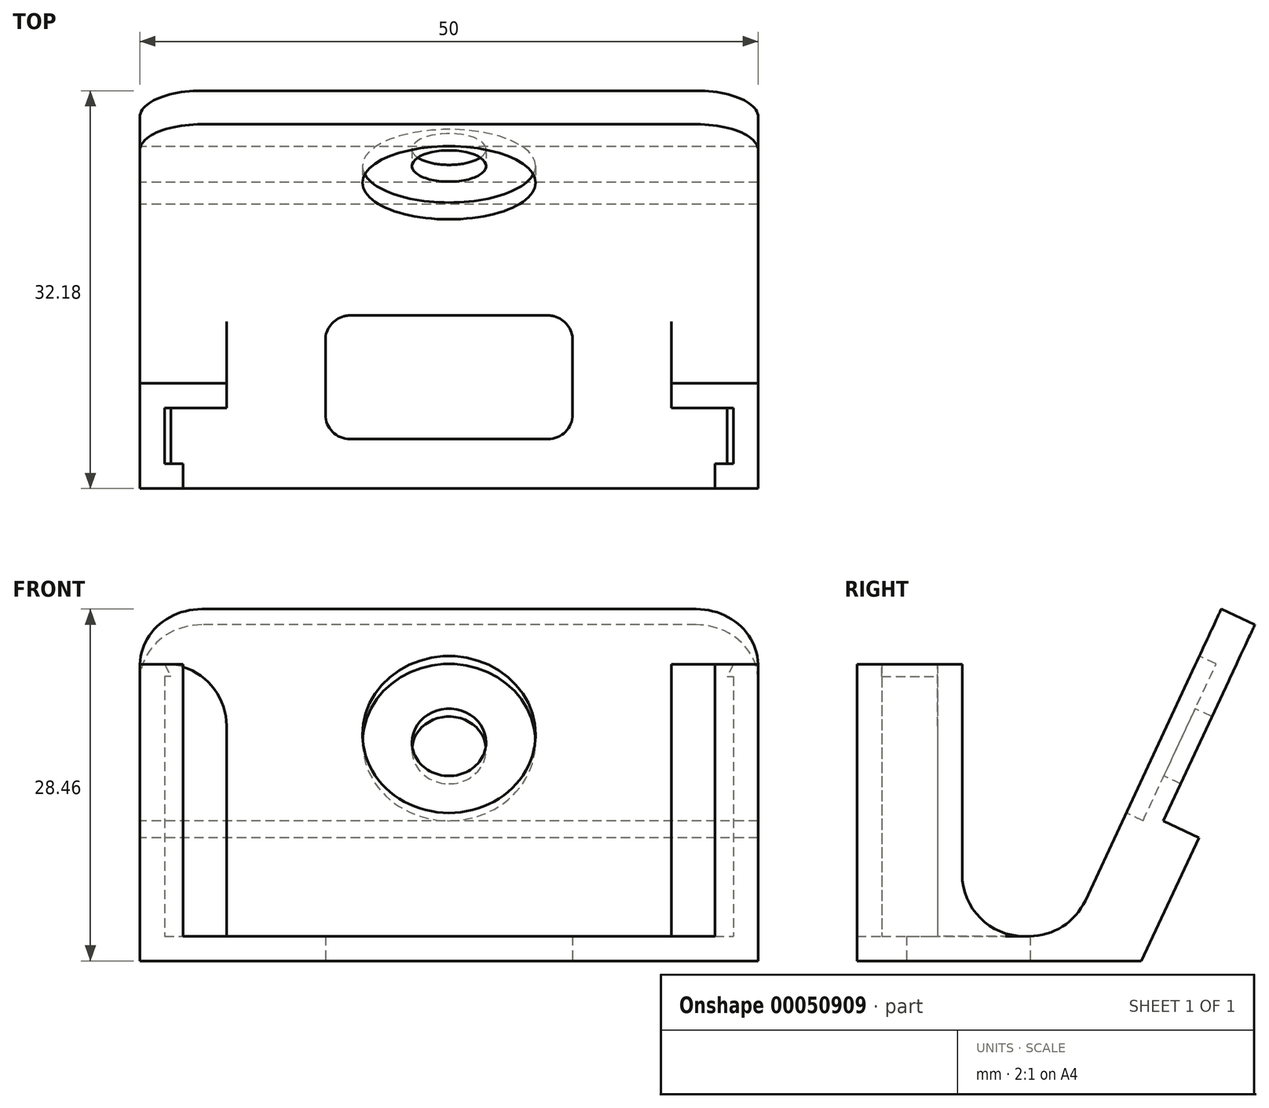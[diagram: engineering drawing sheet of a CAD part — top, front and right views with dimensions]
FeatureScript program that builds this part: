
annotation { "Feature Type Name" : "Feature", "Feature Type Description" : "" }
export const myFeature = defineFeature(function(context is Context, id is Id, definition is map)
    precondition{}
    {
        {
            var Q0;
            Q0=qCreatedBy(makeId("Right.planeOp"),FACE);
            var sketch = newSketch(context, id + "F0", { "sketchPlane" : qUnion([Q0])});
            skLineSegment(sketch, "E0.bottom", {"start": v(0, 0) * mm, "end": v(-2, 0) * mm});
            skLineSegment(sketch, "E0.top", {"start": v(0, 24) * mm, "end": v(-2, 24) * mm});
            skLineSegment(sketch, "E0.left", {"start": v(0, 0) * mm, "end": v(0, 24) * mm});
            skLineSegment(sketch, "E0.right", {"start": v(-2, 0) * mm, "end": v(-2, 24) * mm});
            skLineSegment(sketch, "E1.bottom", {"start": v(0, 0) * mm, "end": v(11, 0) * mm});
            skLineSegment(sketch, "E1.top", {"start": v(0, 2) * mm, "end": v(8.62, 2) * mm});
            skLineSegment(sketch, "E1.left", {"start": v(0, 0) * mm, "end": v(0, 2) * mm});
            skLineSegment(sketch, "E2.top", {"start": v(20.96, 28.46) * mm, "end": v(23.68, 27.19) * mm});
            skLineSegment(sketch, "E2.left", {"start": v(8.62, 2) * mm, "end": v(20.96, 28.46) * mm});
            skLineSegment(sketch, "E2.right", {"start": v(11, 0) * mm, "end": v(23.68, 27.19) * mm});
            skLineSegment(sketch, "E3", {"start": v(11, 0) * mm, "end": v(14.5, 0) * mm});
            skLineSegment(sketch, "E4", {"start": v(14.5, 0) * mm, "end": v(19.15, 9.97) * mm});
            skLineSegment(sketch, "E5", {"start": v(19.15, 9.97) * mm, "end": v(16.27, 11.31) * mm});
            skSolve(sketch);
        }
        {
            var Q0;
            Q0=makeQuery(id+"F0.imprint","IMPRINT",FACE,{"disambiguationData":[TD([[makeQuery(id+"F0.imprint","IMPRINT",EDGE,{"derivedFrom":sQuery(id+"F0.wireOp",EDGE,"E0.bottom")}),-1.0]])]});
            var Q1;
            Q1=makeQuery(id+"F0.imprint","IMPRINT",FACE,{"disambiguationData":[TD([[makeQuery(id+"F0.imprint","IMPRINT",EDGE,{"derivedFrom":sQuery(id+"F0.wireOp",EDGE,"E1.bottom")}),1.0]])]});
            var Q2;
            {var subQ0=sQuery(id+"F0.wireOp",EDGE,"E3");Q2=makeQuery(id+"F0.imprint","IMPRINT",FACE,{"disambiguationData":[TD([[makeQuery(id+"F0.imprint","IMPRINT",EDGE,{"derivedFrom":subQ0}),1.0]])]});}
            extrude(context, id + "F1", {"entities" : qUnion([Q0, Q1, Q2]), "depth" : 50 * mm});
        }
        {
            var Q0;
            Q0=makeQuery(id+"F1.opExtrude","SWEPT_FACE",FACE,{"disambiguationData":[OSD([sQuery(id+"F0.wireOp",EDGE,"E2.left")])]});
            var sketch = newSketch(context, id + "F2", { "sketchPlane" : qUnion([Q0])});
            skCircle(sketch, "E6", {"center": v(25, 23.46) * mm, "radius": 3 * mm});
            skLineSegment(sketch, "E7", {"start": v(0, 23.46) * mm, "end": v(50, 23.46) * mm});
            skSolve(sketch);
        }
        {
            var Q0;
            {var subQ0=sQuery(id+"F2.wireOp",EDGE,"E7");var subQ1=sQuery(id+"F2.wireOp",EDGE,"E6");var subQ2=makeQuery(id+"F2.imprint","INTERSECT",VERTEX,{"disambiguationData":[OD(0.0)],"derivedFrom":[subQ1,subQ0]});Q0=makeQuery(id+"F2.imprint","IMPRINT",FACE,{"disambiguationData":[TD([[makeQuery(id+"F2.imprint","IMPRINT",EDGE,{"disambiguationData":[TD([[subQ2,1.0]])],"derivedFrom":subQ1}),1.0]])]});}
            var Q1;
            {var subQ0=sQuery(id+"F2.wireOp",EDGE,"E7");var subQ1=sQuery(id+"F2.wireOp",EDGE,"E6");var subQ2=makeQuery(id+"F2.imprint","INTERSECT",VERTEX,{"disambiguationData":[OD(0.0)],"derivedFrom":[subQ1,subQ0]});Q1=makeQuery(id+"F2.imprint","IMPRINT",FACE,{"disambiguationData":[TD([[makeQuery(id+"F2.imprint","IMPRINT",EDGE,{"disambiguationData":[TD([[subQ2,-1.0]])],"derivedFrom":subQ1}),1.0]])]});}
            extrude(context, id + "F3", {"entities" : qUnion([Q0, Q1]), "operationType" : NewBodyOperationType.REMOVE, "endBound" : BoundingType.UP_TO_NEXT, "oppositeDirection" : true, "depth" : 25.4 * mm});
        }
        {
            var Q0;
            Q0=makeQuery(id+"F1.opExtrude","SWEPT_FACE",FACE,{"disambiguationData":[OSD([sQuery(id+"F0.wireOp",EDGE,"E0.right")])]});
            var sketch = newSketch(context, id + "F4", { "sketchPlane" : qUnion([Q0])});
            skLineSegment(sketch, "E8", {"start": v(2, 24) * mm, "end": v(2, 2) * mm});
            skLineSegment(sketch, "E9", {"start": v(2, 2) * mm, "end": v(48, 2) * mm});
            skLineSegment(sketch, "E10", {"start": v(48, 2) * mm, "end": v(48, 24) * mm});
            skSolve(sketch);
        }
        {
            var Q0;
            {var subQ3=sQuery(id+"F4.wireOp",EDGE,"E8");Q0=makeQuery(id+"F4.imprint","IMPRINT",FACE,{"disambiguationData":[TD([[makeQuery(id+"F4.imprint","IMPRINT",EDGE,{"derivedFrom":subQ3}),-1.0]])]});}
            extrude(context, id + "F5", {"entities" : qUnion([Q0]), "operationType" : NewBodyOperationType.ADD, "depth" : 6.5 * mm});
        }
        {
            var Q0;
            Q0=makeQuery(id+"F5.opExtrude","SWEPT_FACE",FACE,{"disambiguationData":[OSD([sQuery(id+"F4.wireOp",EDGE,"E8")])]});
            var sketch = newSketch(context, id + "F6", { "sketchPlane" : qUnion([Q0])});
            skLineSegment(sketch, "E11", {"start": v(-6.5, 24) * mm, "end": v(-6.5, 2) * mm});
            skSolve(sketch);
        }
        {
            var Q0;
            {var subQ0=sQuery(id+"F6.wireOp",EDGE,"E11");Q0=makeQuery(id+"F6.imprint","IMPRINT",FACE,{"disambiguationData":[TD([[makeQuery(id+"F6.imprint","IMPRINT",EDGE,{"derivedFrom":subQ0}),-1.0]])]});}
            var Q1;
            Q1=makeQuery(id+"F5.opExtrude","SWEPT_FACE",FACE,{"disambiguationData":[OSD([sQuery(id+"F4.wireOp",EDGE,"E10")])]});
            extrude(context, id + "F7", {"entities" : qUnion([Q0, Q1]), "operationType" : NewBodyOperationType.ADD, "depth" : 1.5 * mm});
        }
        {
            var Q0;
            Q0=makeQuery(id+"F5.opExtrude","SWEPT_FACE",FACE,{"disambiguationData":[OSD([sQuery(id+"F4.wireOp",EDGE,"E10")])]});
            var sketch = newSketch(context, id + "F8", { "sketchPlane" : qUnion([Q0])});
            skLineSegment(sketch, "E12", {"start": v(6.5, 24) * mm, "end": v(6.5, 2) * mm});
            skSolve(sketch);
        }
        {
            var Q0;
            {var subQ0=sQuery(id+"F8.wireOp",EDGE,"E12");Q0=makeQuery(id+"F8.imprint","IMPRINT",FACE,{"disambiguationData":[TD([[makeQuery(id+"F8.imprint","IMPRINT",EDGE,{"derivedFrom":subQ0}),1.0]])]});}
            extrude(context, id + "F9", {"entities" : qUnion([Q0]), "operationType" : NewBodyOperationType.ADD, "depth" : 1.5 * mm});
        }
        {
            var Q0;
            Q0=makeQuery(id+"F1.opExtrude","SWEPT_FACE",FACE,{"disambiguationData":[OSD([sQuery(id+"F0.wireOp",EDGE,"E0.right")])]});
            var sketch = newSketch(context, id + "F10", { "sketchPlane" : qUnion([Q0])});
            skLineSegment(sketch, "E13", {"start": v(7, 24) * mm, "end": v(7, 2) * mm});
            skLineSegment(sketch, "E14", {"start": v(43, 24) * mm, "end": v(43, 2) * mm});
            skSolve(sketch);
        }
        {
            var Q0;
            {var subQ0=sQuery(id+"F10.wireOp",EDGE,"E13");Q0=makeQuery(id+"F10.imprint","IMPRINT",FACE,{"disambiguationData":[TD([[makeQuery(id+"F10.imprint","IMPRINT",EDGE,{"derivedFrom":subQ0}),1.0]])]});}
            extrude(context, id + "F11", {"entities" : qUnion([Q0]), "operationType" : NewBodyOperationType.REMOVE, "oppositeDirection" : true, "depth" : 2 * mm});
        }
        {
            var Q0;
            Q0=qCreatedBy(makeId("Top.planeOp"),FACE);
            var sketch = newSketch(context, id + "F12", { "sketchPlane" : qUnion([Q0])});
            skLineSegment(sketch, "E15.bottom", {"start": v(15, 5.5) * mm, "end": v(35, 5.5) * mm});
            skLineSegment(sketch, "E15.top", {"start": v(15, -4.5) * mm, "end": v(35, -4.5) * mm});
            skLineSegment(sketch, "E15.left", {"start": v(15, 5.5) * mm, "end": v(15, -4.5) * mm});
            skLineSegment(sketch, "E15.right", {"start": v(35, 5.5) * mm, "end": v(35, -4.5) * mm});
            skSolve(sketch);
        }
        {
            var Q0;
            Q0=makeQuery(id+"F12.imprint","IMPRINT",FACE,{"disambiguationData":[TD([[makeQuery(id+"F12.imprint","IMPRINT",EDGE,{"derivedFrom":sQuery(id+"F12.wireOp",EDGE,"E15.bottom")}),-1.0]])]});
            extrude(context, id + "F13", {"entities" : qUnion([Q0]), "operationType" : NewBodyOperationType.REMOVE, "endBound" : BoundingType.THROUGH_ALL, "depth" : 25.4 * mm});
        }
        {
            var Q0;
            Q0=makeQuery(id+"F1.opExtrude","SWEPT_EDGE",EDGE,{"disambiguationData":[OSD([sQuery(id+"F0.wireOp",EDGE,"E1.top"),sQuery(id+"F0.wireOp",EDGE,"E2.left")])]});
            fillet(context, id + "F14", {"entities" : qUnion([Q0]), "radius" : 5 * mm, "tangentPropagation" : true, "allowEdgeOverflow" : false});
        }
        {
            var Q0;
            {var subQ1=sQuery(id+"F0.wireOp",EDGE,"E1.top");var subQ2=sQuery(id+"F0.wireOp",EDGE,"E0.left");Q0=makeQuery(id+"F11.boolean.opBoolean","SPLIT",EDGE,{"disambiguationData":[TD([makeQuery(id+"F11.opExtrude","SWEPT_FACE",FACE,{"disambiguationData":[OSD([sQuery(id+"F10.wireOp",EDGE,"E13")])]})])],"derivedFrom":makeQuery(id+"F1.opExtrude","SWEPT_EDGE",EDGE,{"disambiguationData":[OSD([subQ2,subQ1,sQuery(id+"F0.wireOp",EDGE,"E1.left")])]})});}
            var Q1;
            {var subQ1=sQuery(id+"F0.wireOp",EDGE,"E1.top");var subQ2=sQuery(id+"F0.wireOp",EDGE,"E0.left");Q1=makeQuery(id+"F11.boolean.opBoolean","SPLIT",EDGE,{"disambiguationData":[TD([makeQuery(id+"F11.opExtrude","SWEPT_FACE",FACE,{"disambiguationData":[OSD([sQuery(id+"F10.wireOp",EDGE,"E14")])]})])],"derivedFrom":makeQuery(id+"F1.opExtrude","SWEPT_EDGE",EDGE,{"disambiguationData":[OSD([subQ2,subQ1,sQuery(id+"F0.wireOp",EDGE,"E1.left")])]})});}
            fillet(context, id + "F15", {"entities" : qUnion([Q0, Q1]), "radius" : 5 * mm, "tangentPropagation" : true, "allowEdgeOverflow" : false});
        }
        {
            var Q0;
            Q0=makeQuery(id+"F13.boolean.opBoolean","COPY",EDGE,{"derivedFrom":makeQuery(id+"F13.opExtrude","SWEPT_EDGE",EDGE,{"disambiguationData":[OSD([sQuery(id+"F12.wireOp",EDGE,"E15.bottom"),sQuery(id+"F12.wireOp",EDGE,"E15.right")])]})});
            fillet(context, id + "F16", {"entities" : qUnion([Q0]), "radius" : 2 * mm, "tangentPropagation" : true, "allowEdgeOverflow" : false});
        }
        {
            var Q0;
            Q0=makeQuery(id+"F13.boolean.opBoolean","COPY",EDGE,{"derivedFrom":makeQuery(id+"F13.opExtrude","SWEPT_EDGE",EDGE,{"disambiguationData":[OSD([sQuery(id+"F12.wireOp",EDGE,"E15.bottom"),sQuery(id+"F12.wireOp",EDGE,"E15.left")])]})});
            var Q1;
            Q1=makeQuery(id+"F13.boolean.opBoolean","COPY",EDGE,{"derivedFrom":makeQuery(id+"F13.opExtrude","SWEPT_EDGE",EDGE,{"disambiguationData":[OSD([sQuery(id+"F12.wireOp",EDGE,"E15.top"),sQuery(id+"F12.wireOp",EDGE,"E15.left")])]})});
            fillet(context, id + "F17", {"entities" : qUnion([Q0, Q1]), "radius" : 2 * mm, "tangentPropagation" : true, "allowEdgeOverflow" : false});
        }
        {
            var Q0;
            Q0=makeQuery(id+"F13.boolean.opBoolean","COPY",EDGE,{"derivedFrom":makeQuery(id+"F13.opExtrude","SWEPT_EDGE",EDGE,{"disambiguationData":[OSD([sQuery(id+"F12.wireOp",EDGE,"E15.top"),sQuery(id+"F12.wireOp",EDGE,"E15.right")])]})});
            fillet(context, id + "F18", {"entities" : qUnion([Q0]), "radius" : 2 * mm, "tangentPropagation" : true, "allowEdgeOverflow" : false});
        }
        {
            var Q0;
            Q0=makeQuery(id+"F1.opExtrude","SWEPT_FACE",FACE,{"disambiguationData":[OSD([sQuery(id+"F0.wireOp",EDGE,"E2.left")])]});
            var sketch = newSketch(context, id + "F19", { "sketchPlane" : qUnion([Q0])});
            skCircle(sketch, "E16", {"center": v(25, 23.46) * mm, "radius": 7 * mm});
            skSolve(sketch);
        }
        {
            var Q0;
            Q0=makeQuery(id+"F19.imprint","IMPRINT",FACE,{"disambiguationData":[TD([[makeQuery(id+"F19.imprint","IMPRINT",EDGE,{"derivedFrom":sQuery(id+"F19.wireOp",EDGE,"E16")}),1.0]])]});
            extrude(context, id + "F20", {"entities" : qUnion([Q0]), "operationType" : NewBodyOperationType.REMOVE, "oppositeDirection" : true, "depth" : 1.5 * mm});
        }
        {
            var Q0;
            {var subQ0=sQuery(id+"F4.wireOp",EDGE,"E10");var subQ3=sQuery(id+"F0.wireOp",EDGE,"E0.right");Q0=makeQuery(id+"F11.boolean.opBoolean","SPLIT",FACE,{"disambiguationData":[TD([makeQuery(id+"F5.opExtrude","SWEPT_FACE",FACE,{"disambiguationData":[OSD([subQ0])]})])],"derivedFrom":makeQuery(id+"F1.opExtrude","SWEPT_FACE",FACE,{"disambiguationData":[OSD([subQ3])]})});}
            var sketch = newSketch(context, id + "F21", { "sketchPlane" : qUnion([Q0])});
            skLineSegment(sketch, "E17", {"start": v(48, 24) * mm, "end": v(47.5, 23) * mm});
            skLineSegment(sketch, "E18", {"start": v(47.5, 23) * mm, "end": v(48, 23) * mm});
            skLineSegment(sketch, "E19", {"start": v(48, 23) * mm, "end": v(48, 24) * mm});
            skSolve(sketch);
        }
        {
            var Q0;
            Q0=makeQuery(id+"F21.imprint","IMPRINT",FACE,{"disambiguationData":[TD([[makeQuery(id+"F21.imprint","IMPRINT",EDGE,{"derivedFrom":sQuery(id+"F21.wireOp",EDGE,"E17")}),1.0]])]});
            extrude(context, id + "F22", {"entities" : qUnion([Q0]), "operationType" : NewBodyOperationType.ADD, "endBound" : BoundingType.UP_TO_NEXT, "depth" : 25.4 * mm});
        }
        {
            var Q0;
            {var subQ0=sQuery(id+"F4.wireOp",EDGE,"E8");var subQ3=sQuery(id+"F0.wireOp",EDGE,"E0.right");Q0=makeQuery(id+"F11.boolean.opBoolean","SPLIT",FACE,{"disambiguationData":[TD([makeQuery(id+"F5.opExtrude","SWEPT_FACE",FACE,{"disambiguationData":[OSD([subQ0])]})])],"derivedFrom":makeQuery(id+"F1.opExtrude","SWEPT_FACE",FACE,{"disambiguationData":[OSD([subQ3])]})});}
            var sketch = newSketch(context, id + "F23", { "sketchPlane" : qUnion([Q0])});
            skLineSegment(sketch, "E20", {"start": v(2, 24) * mm, "end": v(2.5, 23) * mm});
            skLineSegment(sketch, "E21", {"start": v(2.5, 23) * mm, "end": v(2, 23) * mm});
            skLineSegment(sketch, "E22", {"start": v(2, 23) * mm, "end": v(2, 24) * mm});
            skSolve(sketch);
        }
        {
            var Q0;
            Q0=makeQuery(id+"F23.imprint","IMPRINT",FACE,{"disambiguationData":[TD([[makeQuery(id+"F23.imprint","IMPRINT",EDGE,{"derivedFrom":sQuery(id+"F23.wireOp",EDGE,"E20")}),-1.0]])]});
            extrude(context, id + "F24", {"entities" : qUnion([Q0]), "operationType" : NewBodyOperationType.ADD, "endBound" : BoundingType.UP_TO_NEXT, "depth" : 25.4 * mm});
        }
        {
            var Q0;
            Q0=makeQuery(id+"F1.opExtrude","CAP_EDGE",EDGE,{"disambiguationData":[OSD([sQuery(id+"F0.wireOp",EDGE,"E2.top")])],"isStart":false});
            var Q1;
            Q1=makeQuery(id+"F1.opExtrude","CAP_EDGE",EDGE,{"disambiguationData":[OSD([sQuery(id+"F0.wireOp",EDGE,"E2.top")])],"isStart":true});
            fillet(context, id + "F25", {"entities" : qUnion([Q0, Q1]), "radius" : 5 * mm, "tangentPropagation" : true, "allowEdgeOverflow" : false});
        }
        {
            var Q0;
            Q0=makeQuery(id+"F11.boolean.opBoolean","COPY",EDGE,{"derivedFrom":makeQuery(id+"F11.opExtrude","SWEPT_EDGE",EDGE,{"disambiguationData":[OSD([sQuery(id+"F0.wireOp",EDGE,"E0.top"),sQuery(id+"F0.wireOp",EDGE,"E0.right"),sQuery(id+"F10.wireOp",EDGE,"E13")])]})});
            var Q1;
            Q1=makeQuery(id+"F11.boolean.opBoolean","COPY",EDGE,{"derivedFrom":makeQuery(id+"F11.opExtrude","SWEPT_EDGE",EDGE,{"disambiguationData":[OSD([sQuery(id+"F0.wireOp",EDGE,"E0.top"),sQuery(id+"F0.wireOp",EDGE,"E0.right"),sQuery(id+"F10.wireOp",EDGE,"E14")])]})});
            fillet(context, id + "F26", {"entities" : qUnion([Q0, Q1]), "radius" : 5 * mm, "tangentPropagation" : true, "allowEdgeOverflow" : false});
        }
    });
